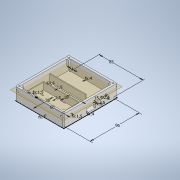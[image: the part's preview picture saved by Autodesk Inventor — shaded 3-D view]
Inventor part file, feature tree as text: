
AUTODESK INVENTOR PART (.ipt)
format: ipt  version: 2022 (Build 260153000, 153)  size: 291,840 bytes
history: native  units: mm
features: extrude x10, sketch x4, other x2, fillet x1
ambient origin geometry x8: Origin, YZ Plane, XZ Plane, XY Plane, X Axis, Y Axis, Z Axis, Center Point
bodies: Body1 (feature_tree)
feature tree (17):
  other  "Těleso1"
  sketch  "Náčrt1"
  extrude  "Vysunutí1"  Depth=4.0mm
  extrude  "Vysunutí2"  Depth=4.0mm
  sketch  "Náčrt2"
  extrude  "Vysunutí5"  Depth=4.0mm
  extrude  "Vysunutí6"  Depth=4.0mm
  other  "Pracovní rovina1"
  extrude  "Vysunutí7"  Depth=85.0mm
  extrude  "Vysunutí8"  Depth=95.0mm
  extrude  "Vysunutí9"  Depth=1.5mm
  fillet  "Zaoblení1"  Radius=69.5mm
  extrude  "Vysunutí10"  Depth=2.5mm
  extrude  "Vysunutí11"  Depth=2.5mm
  extrude  "Vysunutí12"  Depth=15.5mm
  sketch  "Náčrt3"
  sketch  "Náčrt4"
